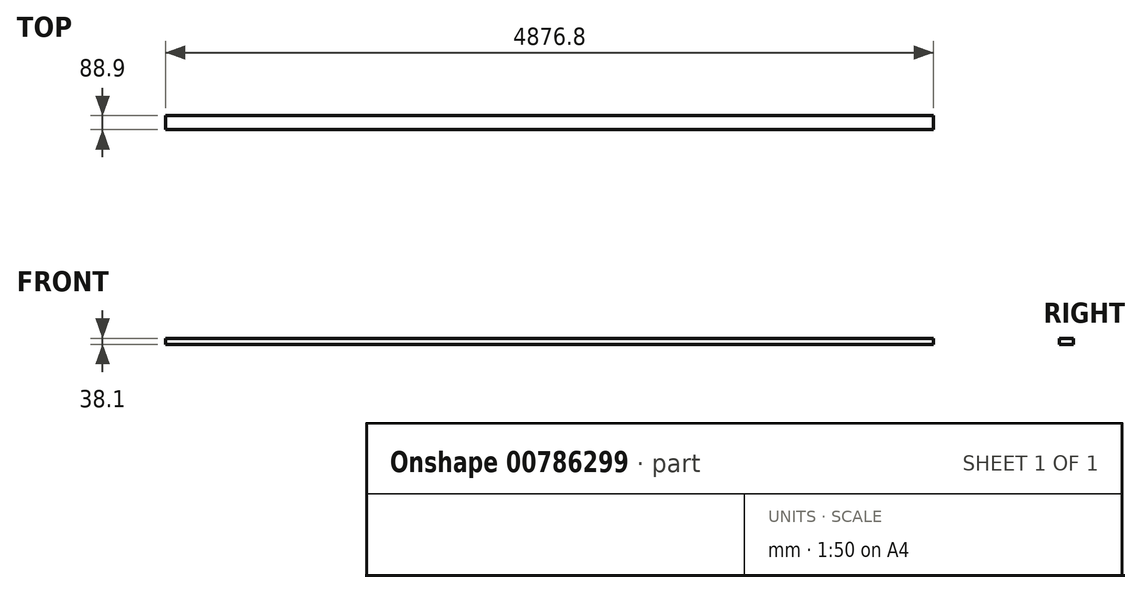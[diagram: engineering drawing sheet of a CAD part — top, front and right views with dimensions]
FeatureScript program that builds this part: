
annotation { "Feature Type Name" : "Feature", "Feature Type Description" : "" }
export const myFeature = defineFeature(function(context is Context, id is Id, definition is map)
    precondition{}
    {
        {
            var Q0;
            Q0=qCreatedBy(makeId("Front.planeOp"),FACE);
            var sketch = newSketch(context, id + "F0", { "sketchPlane" : qUnion([Q0])});
            skLineSegment(sketch, "E0.bottom", {"start": v(-2438.4, 19.05) * mm, "end": v(2438.4, 19.05) * mm});
            skLineSegment(sketch, "E0.top", {"start": v(-2438.4, -19.05) * mm, "end": v(2438.4, -19.05) * mm});
            skLineSegment(sketch, "E0.left", {"start": v(-2438.4, 19.05) * mm, "end": v(-2438.4, -19.05) * mm});
            skLineSegment(sketch, "E0.right", {"start": v(2438.4, 19.05) * mm, "end": v(2438.4, -19.05) * mm});
            skPoint(sketch, "E0.middle", {"position": v(0, 0) * mm});
            skSolve(sketch);
        }
        {
            var Q0;
            Q0=makeQuery(id+"F0.imprint","IMPRINT",FACE,{"disambiguationData":[TD([[makeQuery(id+"F0.imprint","IMPRINT",EDGE,{"derivedFrom":sQuery(id+"F0.wireOp",EDGE,"E0.bottom")}),-1.0]])]});
            extrude(context, id + "F1", {"entities" : qUnion([Q0]), "endBound" : BoundingType.SYMMETRIC, "depth" : 88.9 * mm, "offsetDistance" : 25.4 * mm});
        }
    });
